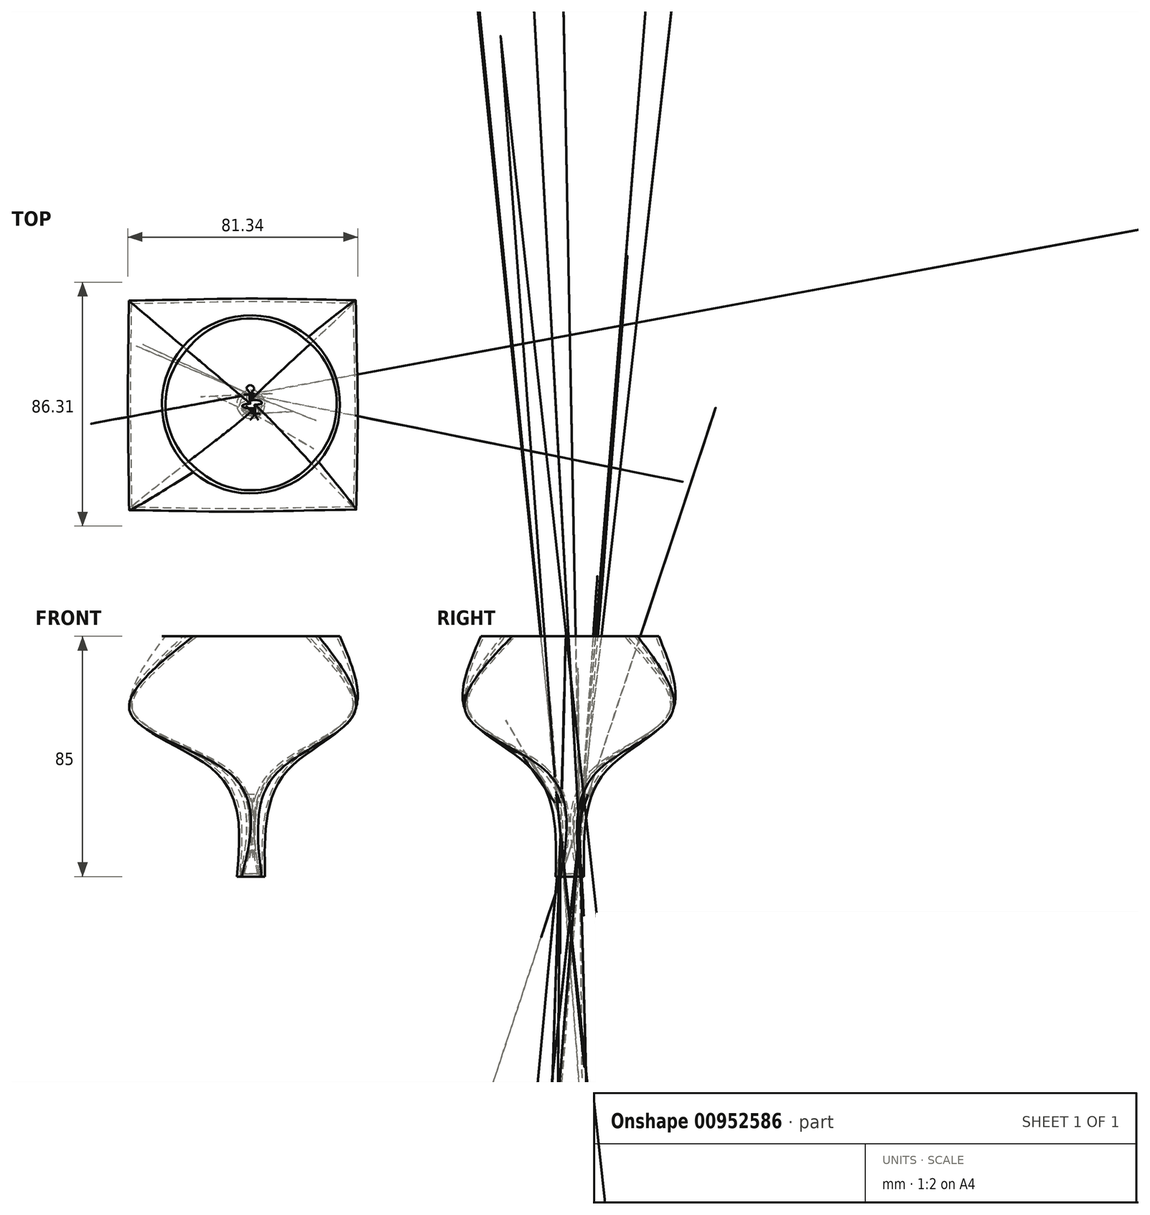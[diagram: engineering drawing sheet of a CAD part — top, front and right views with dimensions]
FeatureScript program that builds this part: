
annotation { "Feature Type Name" : "Feature", "Feature Type Description" : "" }
export const myFeature = defineFeature(function(context is Context, id is Id, definition is map)
    precondition{}
    {
        {
            var Q0;
            Q0=qCreatedBy(makeId("Top.planeOp"),FACE);
            var sketch = newSketch(context, id + "F0", { "sketchPlane" : qUnion([Q0])});
            skCircle(sketch, "E0", {"center": v(0, 0) * mm, "radius": 5 * mm});
            skSolve(sketch);
        }
        {
            var Q0;
            Q0=qCreatedBy(makeId("Top.planeOp"),FACE);
            cPlane(context, id + "F1", {"entities" : qUnion([Q0]), "cplaneType" : CPlaneType.OFFSET, "offset" : 85 * mm, "width" : 150 * mm, "height" : 150 * mm});
        }
        {
            var Q0;
            Q0=qCreatedBy(id+"F1.planeOp",FACE);
            var sketch = newSketch(context, id + "F2", { "sketchPlane" : qUnion([Q0])});
            skCircle(sketch, "E1", {"center": v(0, 0) * mm, "radius": 31.5 * mm});
            skSolve(sketch);
        }
        {
            var Q0;
            Q0=qCreatedBy(makeId("Top.planeOp"),FACE);
            cPlane(context, id + "F3", {"entities" : qUnion([Q0]), "cplaneType" : CPlaneType.OFFSET, "offset" : 37 * mm, "width" : 150 * mm, "height" : 150 * mm});
        }
        {
            var Q0;
            Q0=qCreatedBy(makeId("Top.planeOp"),FACE);
            cPlane(context, id + "F4", {"entities" : qUnion([Q0]), "cplaneType" : CPlaneType.OFFSET, "offset" : 59 * mm, "width" : 150 * mm, "height" : 150 * mm});
        }
        {
            var Q0;
            Q0=qCreatedBy(id+"F3.planeOp",FACE);
            var sketch = newSketch(context, id + "F5", { "sketchPlane" : qUnion([Q0])});
            skCircle(sketch, "E2", {"center": v(0, 0) * mm, "radius": 12.5 * mm});
            skSolve(sketch);
        }
        {
            var Q0;
            Q0=qCreatedBy(id+"F4.planeOp",FACE);
            var sketch = newSketch(context, id + "F6", { "sketchPlane" : qUnion([Q0])});
            skLineSegment(sketch, "E3.bottom", {"start": v(-42.98, 36.54) * mm, "end": v(36.97, 36.54) * mm});
            skLineSegment(sketch, "E3.top", {"start": v(-42.98, -37.1) * mm, "end": v(36.97, -37.1) * mm});
            skLineSegment(sketch, "E3.left", {"start": v(-42.98, 36.54) * mm, "end": v(-42.98, -37.1) * mm});
            skLineSegment(sketch, "E3.right", {"start": v(36.97, 36.54) * mm, "end": v(36.97, -37.1) * mm});
            skSolve(sketch);
        }
        {
            var Q0;
            Q0=qCreatedBy(makeId("Top.planeOp"),FACE);
            cPlane(context, id + "F7", {"entities" : qUnion([Q0]), "cplaneType" : CPlaneType.OFFSET, "offset" : 3.1 * mm, "oppositeDirection" : true, "width" : 150 * mm, "height" : 150 * mm});
        }
        {
            var Q0;
            Q0=makeQuery(id+"F0.imprint","IMPRINT",FACE,{"disambiguationData":[TD([[makeQuery(id+"F0.imprint","IMPRINT",EDGE,{"derivedFrom":sQuery(id+"F0.wireOp",EDGE,"E0")}),1.0]])]});
            var Q1;
            Q1=makeQuery(id+"F5.imprint","IMPRINT",FACE,{"disambiguationData":[TD([[makeQuery(id+"F5.imprint","IMPRINT",EDGE,{"derivedFrom":sQuery(id+"F5.wireOp",EDGE,"E2")}),1.0]])]});
            var Q2;
            Q2=makeQuery(id+"F6.imprint","IMPRINT",FACE,{"disambiguationData":[TD([[makeQuery(id+"F6.imprint","IMPRINT",EDGE,{"derivedFrom":sQuery(id+"F6.wireOp",EDGE,"E3.bottom")}),-1.0]])]});
            var Q3;
            Q3=makeQuery(id+"F2.imprint","IMPRINT",FACE,{"disambiguationData":[TD([[makeQuery(id+"F2.imprint","IMPRINT",EDGE,{"derivedFrom":sQuery(id+"F2.wireOp",EDGE,"E1")}),1.0]])]});
            loft(context, id + "F8", {"sheetProfilesArray" : [{ "sheetProfileEntities" : qUnion([Q0]) }, { "sheetProfileEntities" : qUnion([Q1]) }, { "sheetProfileEntities" : qUnion([Q2]) }, { "sheetProfileEntities" : qUnion([Q3]) }]});
        }
        {
            var Q0;
            Q0=makeQuery(id+"F8.opLoft","CAP_FACE",FACE,{"disambiguationData":[OSD([makeQuery(id+"F2.imprint","IMPRINT",FACE,{"disambiguationData":[TD([[makeQuery(id+"F2.imprint","IMPRINT",EDGE,{"derivedFrom":sQuery(id+"F2.wireOp",EDGE,"E1")}),1.0]])]})])],"isStart":true});
            shell(context, id + "F9", {"entities" : qUnion([Q0]), "thickness" : 1 * mm});
        }
    });
